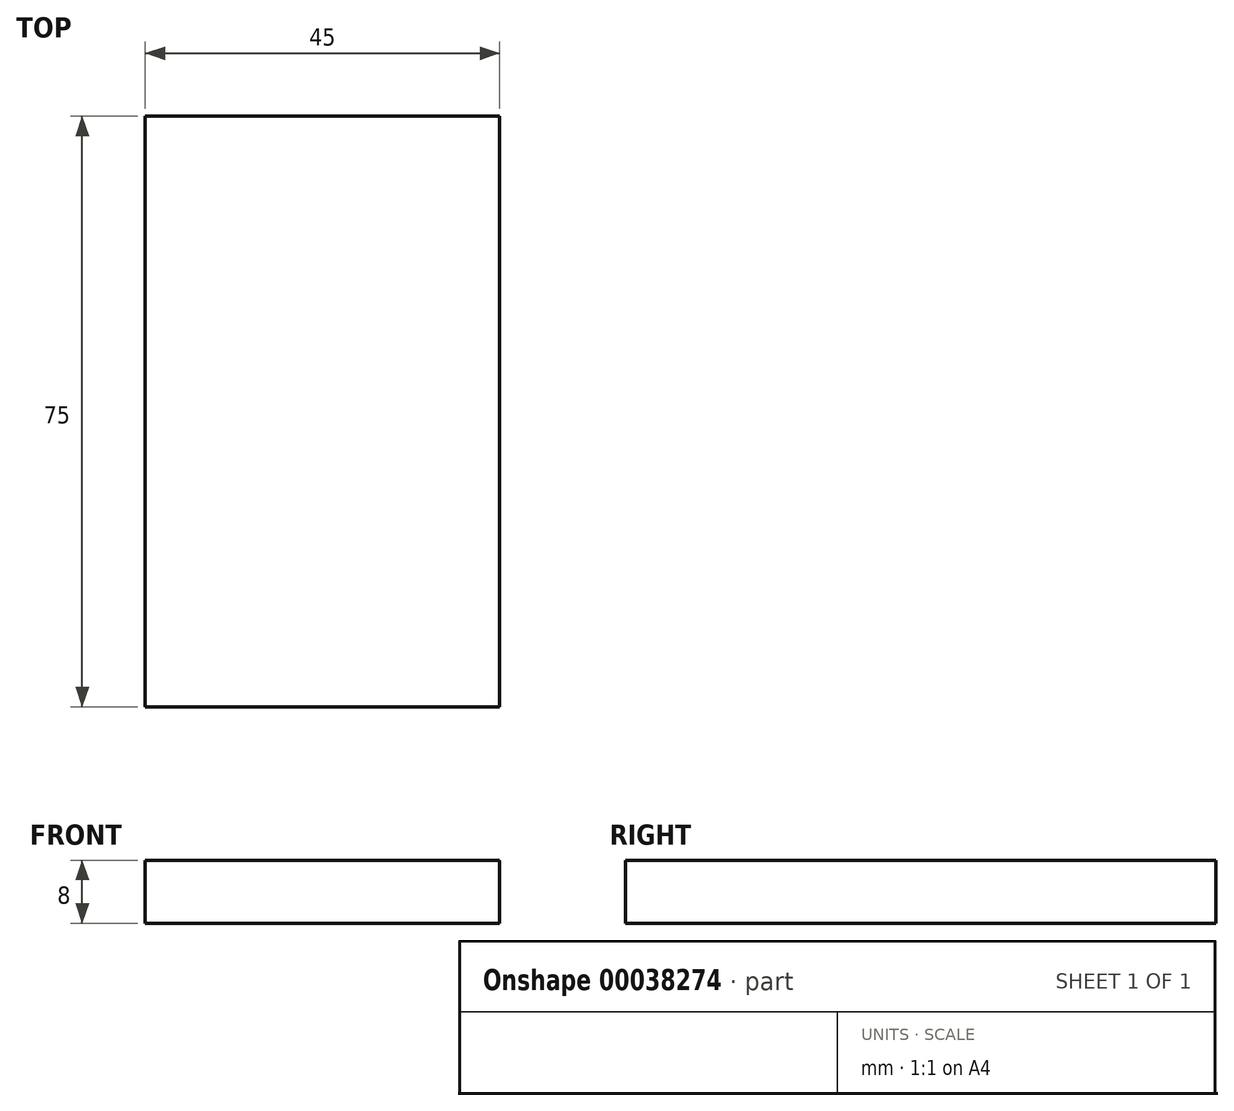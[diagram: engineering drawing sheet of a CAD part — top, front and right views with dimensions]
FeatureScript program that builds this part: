
annotation { "Feature Type Name" : "Feature", "Feature Type Description" : "" }
export const myFeature = defineFeature(function(context is Context, id is Id, definition is map)
    precondition{}
    {
        {
            var Q0;
            Q0=qCreatedBy(makeId("Top.planeOp"),FACE);
            var sketch = newSketch(context, id + "F0", { "sketchPlane" : qUnion([Q0])});
            skLineSegment(sketch, "E0.bottom", {"start": v(-50.9, 18.77) * mm, "end": v(-5.9, 18.77) * mm});
            skLineSegment(sketch, "E0.top", {"start": v(-50.9, -56.23) * mm, "end": v(-5.9, -56.23) * mm});
            skLineSegment(sketch, "E0.left", {"start": v(-50.9, 18.77) * mm, "end": v(-50.9, -56.23) * mm});
            skLineSegment(sketch, "E0.right", {"start": v(-5.9, 18.77) * mm, "end": v(-5.9, -56.23) * mm});
            skLineSegment(sketch, "E1", {"start": v(-50.9, 18.77) * mm, "end": v(-5.9, 18.77) * mm, "construction": true});
            skLineSegment(sketch, "E2", {"start": v(-28.4, 18.77) * mm, "end": v(-28.4, -56.23) * mm, "construction": true});
            skLineSegment(sketch, "E3", {"start": v(-28.4, -56.23) * mm, "end": v(-28.4, -18.73) * mm, "construction": true});
            skLineSegment(sketch, "E4.bottom", {"start": v(-48.4, 16.27) * mm, "end": v(-8.4, 16.27) * mm});
            skLineSegment(sketch, "E4.top", {"start": v(-48.4, -23.73) * mm, "end": v(-8.4, -23.73) * mm});
            skLineSegment(sketch, "E4.left", {"start": v(-48.4, 16.27) * mm, "end": v(-48.4, -23.73) * mm});
            skLineSegment(sketch, "E4.right", {"start": v(-8.4, 16.27) * mm, "end": v(-8.4, -23.73) * mm});
            skLineSegment(sketch, "E5", {"start": v(-28.4, -23.73) * mm, "end": v(-28.4, -56.23) * mm, "construction": true});
            skLineSegment(sketch, "E6", {"start": v(-28.4, -39.98) * mm, "end": v(-50.9, -39.98) * mm, "construction": true});
            skLineSegment(sketch, "E7", {"start": v(-50.9, -39.98) * mm, "end": v(-5.9, -39.98) * mm, "construction": true});
            skCircle(sketch, "E8", {"center": v(-28.4, -39.98) * mm, "radius": 12.5 * mm});
            skCircle(sketch, "E9", {"center": v(-28.4, -39.98) * mm, "radius": 6 * mm});
            skLineSegment(sketch, "E10.bottom", {"start": v(-47.5, 15.15) * mm, "end": v(-9.39, 15.15) * mm});
            skLineSegment(sketch, "E10.top", {"start": v(-47.5, -22.74) * mm, "end": v(-9.39, -22.74) * mm});
            skLineSegment(sketch, "E10.left", {"start": v(-47.5, 15.15) * mm, "end": v(-47.5, -22.74) * mm});
            skLineSegment(sketch, "E10.right", {"start": v(-9.39, 15.15) * mm, "end": v(-9.39, -22.74) * mm});
            skLineSegment(sketch, "E11", {"start": v(-28.4, -27.48) * mm, "end": v(-28.4, -28.48) * mm, "construction": true});
            skText(sketch, "E12", { "text": "MENU", "fontName": "OpenSans-Bold.ttf"});
            const initialGuessF0  = {"E12": [-0.02643, -0.02682, 1, 0, 0.0012]};
            skSetInitialGuess(sketch, initialGuessF0);
            skSolve(sketch);
        }
        {
            var Q0;
            Q0=sQuery(id+"F0.wireOp",EDGE,"E0.bottom");
            var Q1;
            Q1=sQuery(id+"F0.wireOp",EDGE,"E0.left");
            var Q2;
            Q2=sQuery(id+"F0.wireOp",EDGE,"E0.right");
            var Q3;
            Q3=sQuery(id+"F0.wireOp",EDGE,"E0.top");
            extrude(context, id + "F1", {"bodyType" : ToolBodyType.SURFACE, "surfaceEntities" : qUnion([Q0, Q1, Q2, Q3]), "oppositeDirection" : true, "depth" : 8 * mm});
        }
    });
